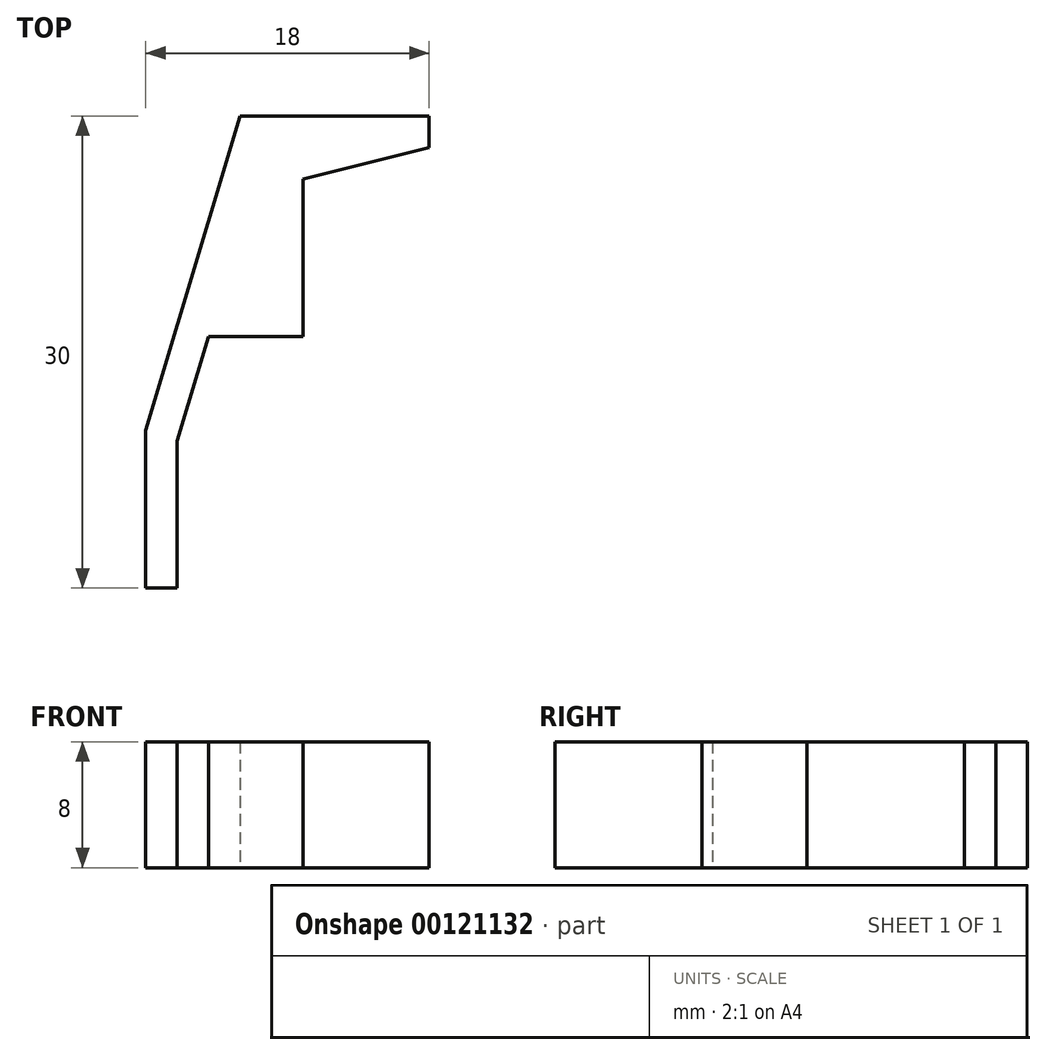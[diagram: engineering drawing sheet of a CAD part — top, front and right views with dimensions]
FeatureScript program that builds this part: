
annotation { "Feature Type Name" : "Feature", "Feature Type Description" : "" }
export const myFeature = defineFeature(function(context is Context, id is Id, definition is map)
    precondition{}
    {
        {
            var Q0;
            Q0=qCreatedBy(makeId("Top.planeOp"),FACE);
            var sketch = newSketch(context, id + "F0", { "sketchPlane" : qUnion([Q0])});
            skLineSegment(sketch, "E0", {"start": v(0, 0) * mm, "end": v(12, 0) * mm});
            skLineSegment(sketch, "E1", {"start": v(12, 0) * mm, "end": v(12, -2) * mm});
            skLineSegment(sketch, "E2", {"start": v(12, -2) * mm, "end": v(4, -2) * mm, "construction": true});
            skLineSegment(sketch, "E3", {"start": v(4, -2) * mm, "end": v(4, -4) * mm, "construction": true});
            skLineSegment(sketch, "E4", {"start": v(12, -2) * mm, "end": v(4, -4) * mm});
            skLineSegment(sketch, "E5", {"start": v(4, -4) * mm, "end": v(4, -14) * mm});
            skLineSegment(sketch, "E6", {"start": v(4, -14) * mm, "end": v(-2, -14) * mm});
            skLineSegment(sketch, "E7", {"start": v(0, 0) * mm, "end": v(0, -20) * mm, "construction": true});
            skLineSegment(sketch, "E8", {"start": v(0, -20) * mm, "end": v(-6, -20) * mm, "construction": true});
            skLineSegment(sketch, "E9", {"start": v(0, 0) * mm, "end": v(-6, -20) * mm});
            skLineSegment(sketch, "E10", {"start": v(-6, -20) * mm, "end": v(-6, -30) * mm});
            skLineSegment(sketch, "E11", {"start": v(-6, -30) * mm, "end": v(-4, -30) * mm});
            skLineSegment(sketch, "E12", {"start": v(-4, -30) * mm, "end": v(-4, -18.4) * mm, "construction": true});
            skLineSegment(sketch, "E13", {"start": v(-2, -14) * mm, "end": v(-7.75, -33.16) * mm, "construction": true});
            skLineSegment(sketch, "E14", {"start": v(-2, -14) * mm, "end": v(-4, -20.67) * mm});
            skLineSegment(sketch, "E15", {"start": v(-4, -20.67) * mm, "end": v(-4, -30) * mm});
            skLineSegment(sketch, "E16", {"start": v(4, -14) * mm, "end": v(4, -30) * mm, "construction": true});
            skSolve(sketch);
        }
        {
            var Q0;
            Q0 = qSketchRegion(id + "F0", true);
            extrude(context, id + "F1", {"entities" : qUnion([Q0]), "depth" : 8 * mm});
        }
    });
